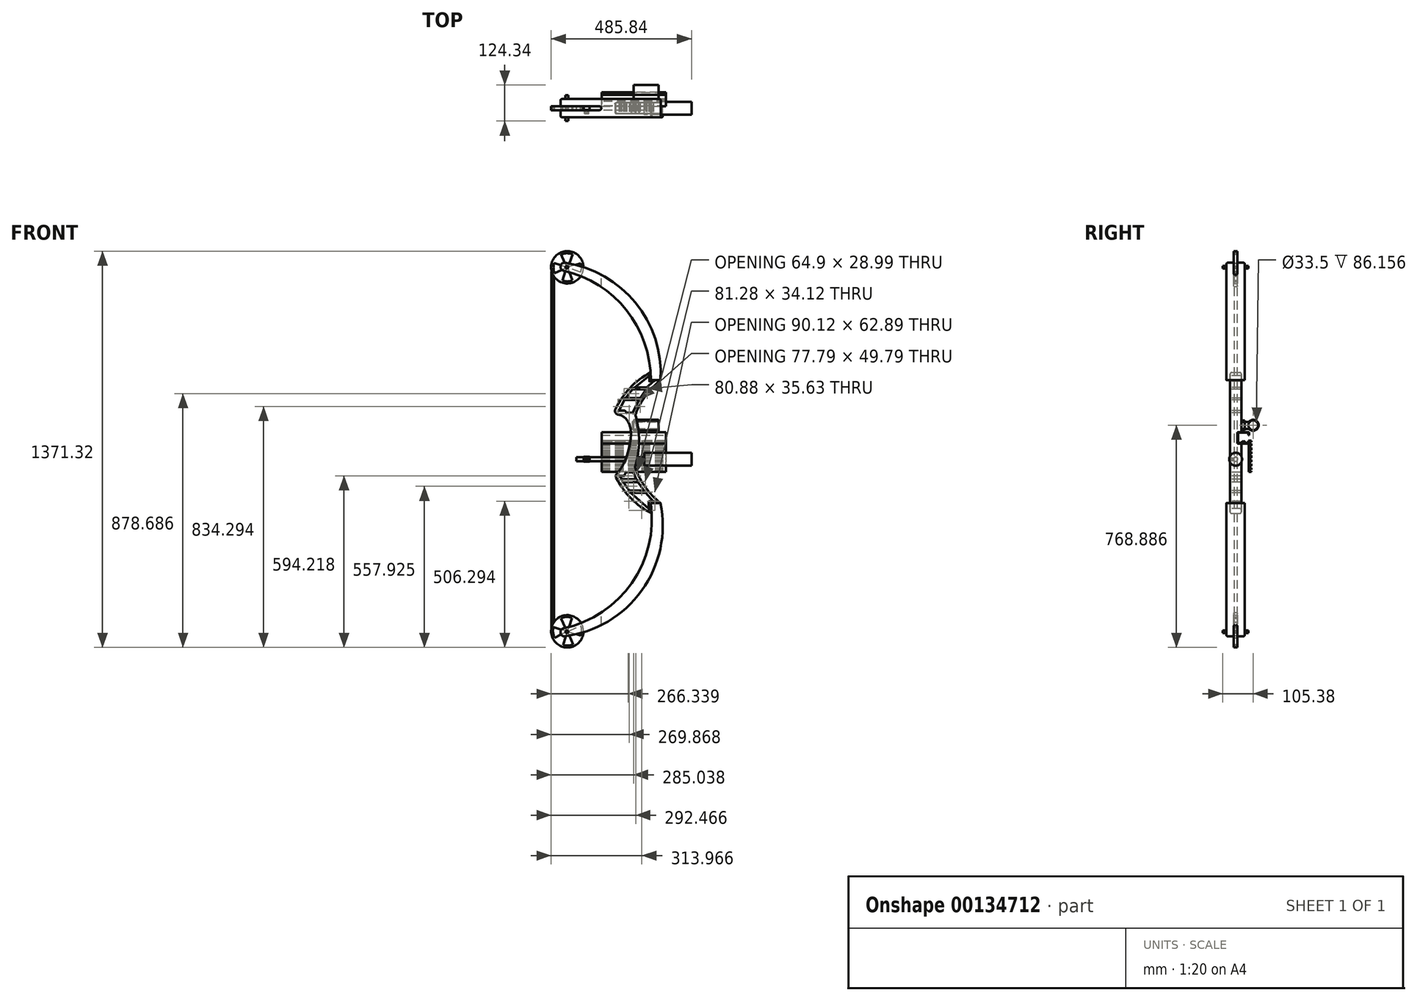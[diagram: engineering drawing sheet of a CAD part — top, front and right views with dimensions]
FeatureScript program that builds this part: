
annotation { "Feature Type Name" : "Feature", "Feature Type Description" : "" }
export const myFeature = defineFeature(function(context is Context, id is Id, definition is map)
    precondition{}
    {
        {
            var Q0;
            Q0=qCreatedBy(makeId("Front.planeOp"),FACE);
            var sketch = newSketch(context, id + "F0", { "sketchPlane" : qUnion([Q0])});
            skArc(sketch, "E0", {"start": v(312.15, 225.22) * mm, "mid": v(224.63, 471.96) * mm, "end": v(0, 606.44) * mm});
            skArc(sketch, "E1", {"start": v(0, -635.15) * mm, "mid": v(243.69, -480.2) * mm, "end": v(312.15, -199.65) * mm});
            skLineSegment(sketch, "E2", {"start": v(0, 606.44) * mm, "end": v(0, 633.37) * mm});
            skLineSegment(sketch, "E3", {"start": v(0, -635.15) * mm, "end": v(0, -662.07) * mm});
            skLineSegment(sketch, "E4", {"start": v(312.15, 225.22) * mm, "end": v(345.94, 225.22) * mm});
            skLineSegment(sketch, "E5", {"start": v(312.15, -199.65) * mm, "end": v(345.93, -199.65) * mm});
            skArc(sketch, "E6", {"start": v(345.94, 225.22) * mm, "mid": v(254.91, 498.75) * mm, "end": v(0, 633.37) * mm});
            skArc(sketch, "E7", {"start": v(0, -662.07) * mm, "mid": v(276.6, -508.4) * mm, "end": v(345.93, -199.65) * mm});
            skSolve(sketch);
        }
        {
            var Q0;
            Q0=qSketchRegion(id+"F0",true);
            extrude(context, id + "F1", {"entities" : qUnion([Q0]), "depth" : 38.1 * mm, "hasSecondDirection" : true, "secondDirectionOppositeDirection" : true, "secondDirectionDepth" : 25.4 * mm});
        }
        {
            var Q0;
            Q0=qCreatedBy(makeId("Front.planeOp"),FACE);
            var sketch = newSketch(context, id + "F2", { "sketchPlane" : qUnion([Q0])});
            skArc(sketch, "E8", {"start": v(328.65, 260.2) * mm, "mid": v(164.15, 6.75) * mm, "end": v(333.35, -243.58) * mm});
            skArc(sketch, "E9", {"start": v(345.8, 225.54) * mm, "mid": v(242.77, 13.02) * mm, "end": v(345.76, -199.52) * mm});
            skLineSegment(sketch, "E10", {"start": v(333.35, -243.58) * mm, "end": v(345.76, -199.52) * mm});
            skLineSegment(sketch, "E11", {"start": v(328.65, 260.2) * mm, "end": v(345.8, 225.54) * mm});
            skArc(sketch, "E12", {"start": v(257.5, -75.1) * mm, "mid": v(271.65, 14.65) * mm, "end": v(258.73, 104.58) * mm});
            skArc(sketch, "E13", {"start": v(176.09, -70.66) * mm, "mid": v(193.2, 15.9) * mm, "end": v(180.78, 103.27) * mm});
            skSolve(sketch);
        }
        {
            var Q0;
            Q0=qSketchRegion(id+"F2",true);
            extrude(context, id + "F3", {"entities" : qUnion([Q0]), "operationType" : NewBodyOperationType.ADD, "depth" : 25.4 * mm, "hasSecondDirection" : true, "secondDirectionOppositeDirection" : true, "secondDirectionDepth" : 13.4 * mm});
        }
        {
            var Q0;
            Q0=qSketchRegion(id+"F2",true);
            extrude(context, id + "F4", {"entities" : qUnion([Q0]), "operationType" : NewBodyOperationType.ADD, "depth" : 25.4 * mm});
        }
        {
            var Q0;
            Q0=qCreatedBy(makeId("Front.planeOp"),FACE);
            var sketch = newSketch(context, id + "F5", { "sketchPlane" : qUnion([Q0])});
            skFitSpline(sketch, "E14", {"points": [v(182.57, 103.7) * mm, v(240.87, 63.55) * mm, v(188.22, -101.45) * mm, v(156.8, -24.45) * mm, v(182.57, 103.7) * mm]});
            skSolve(sketch);
        }
        {
            var Q0;
            Q0=qSketchRegion(id+"F5",true);
            extrude(context, id + "F6", {"entities" : qUnion([Q0]), "operationType" : NewBodyOperationType.REMOVE, "oppositeDirection" : true, "depth" : 25.4 * mm, "hasSecondDirection" : true, "secondDirectionOppositeDirection" : false, "secondDirectionDepth" : 25.4 * mm});
        }
        {
            var Q0;
            {var subQ0=sQuery(id+"F2.wireOp",EDGE,"E8");Q0=makeQuery(id+"F6.boolean.opBoolean","INTERSECT",EDGE,{"disambiguationData":[OD(0.0)],"derivedFrom":[makeQuery(id+"F4.boolean.opBoolean","MERGE",FACE,{"derivedFrom":[makeQuery(id+"F3.opExtrude","SWEPT_FACE",FACE,{"disambiguationData":[OSD([subQ0])]}),makeQuery(id+"F4.opExtrude","SWEPT_FACE",FACE,{"disambiguationData":[OSD([subQ0])]})]}),makeQuery(id+"F6.opExtrude","SWEPT_FACE",FACE,{"disambiguationData":[OSD([sQuery(id+"F5.wireOp",EDGE,"E14")])]})]});}
            var Q1;
            {var subQ0=sQuery(id+"F2.wireOp",EDGE,"E8");Q1=makeQuery(id+"F6.boolean.opBoolean","INTERSECT",EDGE,{"disambiguationData":[OD(1.0)],"derivedFrom":[makeQuery(id+"F4.boolean.opBoolean","MERGE",FACE,{"derivedFrom":[makeQuery(id+"F3.opExtrude","SWEPT_FACE",FACE,{"disambiguationData":[OSD([subQ0])]}),makeQuery(id+"F4.opExtrude","SWEPT_FACE",FACE,{"disambiguationData":[OSD([subQ0])]})]}),makeQuery(id+"F6.opExtrude","SWEPT_FACE",FACE,{"disambiguationData":[OSD([sQuery(id+"F5.wireOp",EDGE,"E14")])]})]});}
            var Q2;
            {var subQ0=sQuery(id+"F2.wireOp",EDGE,"E12");var subQ1=sQuery(id+"F2.wireOp",EDGE,"E9");var subQ2=makeQuery(id+"F2.imprint","INTERSECT",VERTEX,{"disambiguationData":[OD(1.0)],"derivedFrom":[subQ1,subQ0]});Q2=makeQuery(id+"F4.boolean.opBoolean","MERGE",EDGE,{"derivedFrom":[makeQuery(id+"F3.opExtrude","SWEPT_EDGE",EDGE,{"disambiguationData":[OSD([subQ1,subQ0]),TDD([subQ2])]}),makeQuery(id+"F4.opExtrude","SWEPT_EDGE",EDGE,{"disambiguationData":[OSD([subQ1,subQ0]),TDD([subQ2])]})]});}
            var Q3;
            {var subQ0=sQuery(id+"F2.wireOp",EDGE,"E12");var subQ1=sQuery(id+"F2.wireOp",EDGE,"E9");var subQ2=makeQuery(id+"F2.imprint","INTERSECT",VERTEX,{"disambiguationData":[OD(0.0)],"derivedFrom":[subQ1,subQ0]});Q3=makeQuery(id+"F4.boolean.opBoolean","MERGE",EDGE,{"derivedFrom":[makeQuery(id+"F3.opExtrude","SWEPT_EDGE",EDGE,{"disambiguationData":[OSD([subQ1,subQ0]),TDD([subQ2])]}),makeQuery(id+"F4.opExtrude","SWEPT_EDGE",EDGE,{"disambiguationData":[OSD([subQ1,subQ0]),TDD([subQ2])]})]});}
            var Q4;
            Q4=makeQuery(id+"F1.opExtrude","SWEPT_EDGE",EDGE,{"disambiguationData":[OSD([sQuery(id+"F0.wireOp",EDGE,"E3"),sQuery(id+"F0.wireOp",EDGE,"E7")])]});
            var Q5;
            Q5=makeQuery(id+"F1.opExtrude","SWEPT_EDGE",EDGE,{"disambiguationData":[OSD([sQuery(id+"F0.wireOp",EDGE,"E1"),sQuery(id+"F0.wireOp",EDGE,"E3")])]});
            var Q6;
            Q6=makeQuery(id+"F1.opExtrude","SWEPT_EDGE",EDGE,{"disambiguationData":[OSD([sQuery(id+"F0.wireOp",EDGE,"E0"),sQuery(id+"F0.wireOp",EDGE,"E2")])]});
            var Q7;
            Q7=makeQuery(id+"F1.opExtrude","SWEPT_EDGE",EDGE,{"disambiguationData":[OSD([sQuery(id+"F0.wireOp",EDGE,"E2"),sQuery(id+"F0.wireOp",EDGE,"E6")])]});
            fillet(context, id + "F7", {"entities" : qUnion([Q0, Q1, Q2, Q3, Q4, Q5, Q6, Q7]), "radius" : 12.7 * mm, "tangentPropagation" : true, "allowEdgeOverflow" : false});
        }
        {
            var Q0;
            Q0=makeQuery(id+"F1.opExtrude","CAP_EDGE",EDGE,{"disambiguationData":[OSD([sQuery(id+"F0.wireOp",EDGE,"E0")])],"isStart":false});
            var Q1;
            Q1=makeQuery(id+"F1.opExtrude","CAP_EDGE",EDGE,{"disambiguationData":[OSD([sQuery(id+"F0.wireOp",EDGE,"E0")])],"isStart":true});
            var Q2;
            {var subQ0=sQuery(id+"F2.wireOp",EDGE,"E8");Q2=makeQuery(id+"F6.boolean.opBoolean","SPLIT",EDGE,{"disambiguationData":[TD([makeQuery(id+"F1.opExtrude","SWEPT_FACE",FACE,{"disambiguationData":[OSD([sQuery(id+"F0.wireOp",EDGE,"E0")])]})])],"derivedFrom":makeQuery(id+"F3.opExtrude","CAP_EDGE",EDGE,{"disambiguationData":[OSD([subQ0])],"isStart":true})});}
            var Q3;
            {var subQ0=sQuery(id+"F2.wireOp",EDGE,"E9");Q3=makeQuery(id+"F3.opExtrude","CAP_EDGE",EDGE,{"disambiguationData":[OSD([subQ0]),TDD([makeQuery(id+"F2.imprint","IMPRINT",EDGE,{"disambiguationData":[TD([[makeQuery(id+"F2.imprint","INTERSECT",VERTEX,{"derivedFrom":[subQ0,sQuery(id+"F2.wireOp",EDGE,"E11")]}),-1.0]])],"derivedFrom":subQ0})])],"isStart":true});}
            var Q4;
            {var subQ0=sQuery(id+"F2.wireOp",EDGE,"E8");Q4=makeQuery(id+"F6.boolean.opBoolean","SPLIT",EDGE,{"disambiguationData":[TD([makeQuery(id+"F1.opExtrude","SWEPT_FACE",FACE,{"disambiguationData":[OSD([sQuery(id+"F0.wireOp",EDGE,"E0")])]})])],"derivedFrom":makeQuery(id+"F3.opExtrude","CAP_EDGE",EDGE,{"disambiguationData":[OSD([subQ0])],"isStart":false})});}
            var Q5;
            {var subQ0=sQuery(id+"F2.wireOp",EDGE,"E9");Q5=makeQuery(id+"F3.opExtrude","CAP_EDGE",EDGE,{"disambiguationData":[OSD([subQ0]),TDD([makeQuery(id+"F2.imprint","IMPRINT",EDGE,{"disambiguationData":[TD([[makeQuery(id+"F2.imprint","INTERSECT",VERTEX,{"derivedFrom":[subQ0,sQuery(id+"F2.wireOp",EDGE,"E11")]}),-1.0]])],"derivedFrom":subQ0})])],"isStart":false});}
            var Q6;
            Q6=makeQuery(id+"F1.opExtrude","CAP_EDGE",EDGE,{"disambiguationData":[OSD([sQuery(id+"F0.wireOp",EDGE,"E1")])],"isStart":true});
            var Q7;
            Q7=makeQuery(id+"F1.opExtrude","CAP_EDGE",EDGE,{"disambiguationData":[OSD([sQuery(id+"F0.wireOp",EDGE,"E1")])],"isStart":false});
            fillet(context, id + "F8", {"entities" : qUnion([Q0, Q1, Q2, Q3, Q4, Q5, Q6, Q7]), "radius" : 5.08 * mm, "tangentPropagation" : true, "allowEdgeOverflow" : false});
        }
        {
            var Q0;
            Q0=qCreatedBy(makeId("Top.planeOp"),FACE);
            var sketch = newSketch(context, id + "F9", { "sketchPlane" : qUnion([Q0])});
            skLineSegment(sketch, "E15", {"start": v(0, 0) * mm, "end": v(134.72, 0) * mm});
            skLineSegment(sketch, "E16", {"start": v(0, -12.95) * mm, "end": v(134.72, -12.95) * mm});
            skArc(sketch, "E17", {"start": v(134.72, -12.95) * mm, "mid": v(141.2, -6.48) * mm, "end": v(134.72, 0) * mm});
            skLineSegment(sketch, "E18", {"start": v(0, 0) * mm, "end": v(0, -12.95) * mm});
            skSolve(sketch);
        }
        {
            var Q0;
            Q0=qSketchRegion(id+"F9",true);
            extrude(context, id + "F10", {"entities" : qUnion([Q0]), "operationType" : NewBodyOperationType.REMOVE, "oppositeDirection" : true, "depth" : 1043.23 * mm, "hasSecondDirection" : true, "secondDirectionOppositeDirection" : false, "secondDirectionDepth" : 725.43 * mm});
        }
        {
            var Q0;
            Q0=qCreatedBy(makeId("Front.planeOp"),FACE);
            var sketch = newSketch(context, id + "F11", { "sketchPlane" : qUnion([Q0])});
            skLineSegment(sketch, "E19", {"start": v(307.3, 240.65) * mm, "end": v(307.3, 221.5) * mm});
            skLineSegment(sketch, "E20", {"start": v(307.3, 221.5) * mm, "end": v(321.6, 221.5) * mm});
            skLineSegment(sketch, "E21", {"start": v(321.6, 221.5) * mm, "end": v(299.17, 200.17) * mm});
            skLineSegment(sketch, "E22", {"start": v(299.17, 200.17) * mm, "end": v(257.15, 200.17) * mm});
            skLineSegment(sketch, "E23", {"start": v(257.15, 200.17) * mm, "end": v(307.3, 240.65) * mm});
            skLineSegment(sketch, "E24", {"start": v(249.41, 194.56) * mm, "end": v(295.62, 194.56) * mm});
            skLineSegment(sketch, "E25", {"start": v(295.62, 194.56) * mm, "end": v(275.44, 164.01) * mm});
            skLineSegment(sketch, "E26", {"start": v(275.44, 164.01) * mm, "end": v(224.78, 164.01) * mm});
            skLineSegment(sketch, "E27", {"start": v(224.78, 164.01) * mm, "end": v(249.41, 194.56) * mm});
            skLineSegment(sketch, "E28", {"start": v(221.45, 157.23) * mm, "end": v(202.6, 120.92) * mm});
            skLineSegment(sketch, "E29", {"start": v(202.6, 120.92) * mm, "end": v(222.32, 120.92) * mm});
            skLineSegment(sketch, "E30", {"start": v(222.32, 120.92) * mm, "end": v(228.43, 112.54) * mm});
            skLineSegment(sketch, "E31", {"start": v(228.43, 112.54) * mm, "end": v(249.56, 112.54) * mm});
            skLineSegment(sketch, "E32", {"start": v(249.56, 112.54) * mm, "end": v(272.08, 156.7) * mm});
            skLineSegment(sketch, "E33", {"start": v(272.08, 156.7) * mm, "end": v(221.45, 157.23) * mm});
            skSolve(sketch);
        }
        {
            var Q0;
            Q0=qSketchRegion(id+"F11",true);
            extrude(context, id + "F12", {"entities" : qUnion([Q0]), "operationType" : NewBodyOperationType.REMOVE, "oppositeDirection" : true, "depth" : 25.4 * mm, "hasSecondDirection" : true, "secondDirectionOppositeDirection" : false, "secondDirectionDepth" : 103.34 * mm});
        }
        {
            var Q0;
            Q0=qCreatedBy(makeId("Front.planeOp"),FACE);
            var sketch = newSketch(context, id + "F13", { "sketchPlane" : qUnion([Q0])});
            skLineSegment(sketch, "E34", {"start": v(304.9, -218.91) * mm, "end": v(304.9, -193.2) * mm});
            skLineSegment(sketch, "E35", {"start": v(304.9, -193.2) * mm, "end": v(320.72, -193.2) * mm});
            skLineSegment(sketch, "E36", {"start": v(320.72, -193.2) * mm, "end": v(294.36, -164.2) * mm});
            skLineSegment(sketch, "E37", {"start": v(294.36, -164.2) * mm, "end": v(243.05, -164.2) * mm});
            skLineSegment(sketch, "E38", {"start": v(243.05, -164.2) * mm, "end": v(304.9, -218.91) * mm});
            skLineSegment(sketch, "E39", {"start": v(288.23, -156) * mm, "end": v(237.22, -156) * mm});
            skLineSegment(sketch, "E40", {"start": v(237.22, -156) * mm, "end": v(216.74, -126.96) * mm});
            skLineSegment(sketch, "E41", {"start": v(216.74, -126.96) * mm, "end": v(267.82, -126.96) * mm});
            skLineSegment(sketch, "E42", {"start": v(267.82, -126.96) * mm, "end": v(288.23, -156) * mm});
            skLineSegment(sketch, "E43", {"start": v(262.27, -117.14) * mm, "end": v(210.93, -117.14) * mm});
            skLineSegment(sketch, "E44", {"start": v(210.93, -117.14) * mm, "end": v(205.44, -106.16) * mm});
            skLineSegment(sketch, "E45", {"start": v(205.44, -106.16) * mm, "end": v(220.33, -106.16) * mm});
            skLineSegment(sketch, "E46", {"start": v(220.33, -106.16) * mm, "end": v(226.6, -93.23) * mm});
            skLineSegment(sketch, "E47", {"start": v(226.6, -93.23) * mm, "end": v(251.3, -93.23) * mm});
            skLineSegment(sketch, "E48", {"start": v(251.3, -93.23) * mm, "end": v(262.27, -117.14) * mm});
            skSolve(sketch);
        }
        {
            var Q0;
            Q0=qSketchRegion(id+"F13",true);
            extrude(context, id + "F14", {"entities" : qUnion([Q0]), "operationType" : NewBodyOperationType.REMOVE, "oppositeDirection" : true, "depth" : 25.4 * mm, "hasSecondDirection" : true, "secondDirectionOppositeDirection" : false, "secondDirectionDepth" : 136.26 * mm});
        }
        {
            var Q0;
            Q0=qCreatedBy(makeId("Front.planeOp"),FACE);
            var sketch = newSketch(context, id + "F15", { "sketchPlane" : qUnion([Q0])});
            skCircle(sketch, "E49", {"center": v(23.33, 616.03) * mm, "radius": 55.9 * mm});
            skCircle(sketch, "E50", {"center": v(23.33, -643.5) * mm, "radius": 55.9 * mm});
            skCircle(sketch, "E51", {"center": v(23.33, 616.03) * mm, "radius": 4.58 * mm});
            skLineSegment(sketch, "E52", {"start": v(19.88, 619.04) * mm, "end": v(2.06, 661.07) * mm});
            skLineSegment(sketch, "E53", {"start": v(26.37, 619.46) * mm, "end": v(42.28, 661.63) * mm});
            skLineSegment(sketch, "E54", {"start": v(20.5, 612.42) * mm, "end": v(6.51, 570.45) * mm});
            skLineSegment(sketch, "E55", {"start": v(26.38, 612.6) * mm, "end": v(40.24, 570.82) * mm});
            skArc(sketch, "E56", {"start": v(42.28, 661.63) * mm, "mid": v(22.13, 664.6) * mm, "end": v(2.06, 661.07) * mm});
            skArc(sketch, "E57", {"start": v(6.51, 570.45) * mm, "mid": v(23.42, 566.64) * mm, "end": v(40.24, 570.82) * mm});
            skLineSegment(sketch, "E58", {"start": v(27.5, 617.94) * mm, "end": v(69.87, 630.2) * mm});
            skLineSegment(sketch, "E59", {"start": v(27.5, 614.11) * mm, "end": v(69.21, 598.67) * mm});
            skLineSegment(sketch, "E60", {"start": v(19.14, 617.87) * mm, "end": v(-22.68, 630.88) * mm});
            skLineSegment(sketch, "E61", {"start": v(19.1, 614.26) * mm, "end": v(-21.29, 595.17) * mm});
            skArc(sketch, "E62", {"start": v(-22.68, 630.88) * mm, "mid": v(-24.57, 612.92) * mm, "end": v(-21.29, 595.17) * mm});
            skArc(sketch, "E63", {"start": v(69.21, 598.67) * mm, "mid": v(72.24, 614.38) * mm, "end": v(69.87, 630.2) * mm});
            skCircle(sketch, "E64", {"center": v(23.33, -643.5) * mm, "radius": 4.58 * mm});
            skLineSegment(sketch, "E65", {"start": v(20.29, -640.08) * mm, "end": v(1.41, -598.57) * mm});
            skLineSegment(sketch, "E66", {"start": v(25.93, -639.73) * mm, "end": v(39.75, -596.96) * mm});
            skLineSegment(sketch, "E67", {"start": v(21.54, -647.73) * mm, "end": v(8.9, -690.96) * mm});
            skLineSegment(sketch, "E68", {"start": v(26, -647.23) * mm, "end": v(44, -688.73) * mm});
            skLineSegment(sketch, "E69", {"start": v(27.8, -642.46) * mm, "end": v(69.69, -624.26) * mm});
            skLineSegment(sketch, "E70", {"start": v(27.47, -645.49) * mm, "end": v(70.34, -658.33) * mm});
            skLineSegment(sketch, "E71", {"start": v(18.96, -642.13) * mm, "end": v(-24.47, -629.13) * mm});
            skLineSegment(sketch, "E72", {"start": v(19.17, -645.42) * mm, "end": v(-19.95, -665.33) * mm});
            skArc(sketch, "E73", {"start": v(39.75, -596.96) * mm, "mid": v(20.4, -593.5) * mm, "end": v(1.41, -598.57) * mm});
            skArc(sketch, "E74", {"start": v(-24.47, -629.13) * mm, "mid": v(-25.69, -647.66) * mm, "end": v(-19.95, -665.33) * mm});
            skArc(sketch, "E75", {"start": v(8.9, -690.96) * mm, "mid": v(26.64, -692.84) * mm, "end": v(44, -688.73) * mm});
            skArc(sketch, "E76", {"start": v(70.34, -658.33) * mm, "mid": v(73.15, -641.24) * mm, "end": v(69.69, -624.26) * mm});
            skSolve(sketch);
        }
        {
            var Q0;
            Q0=qCreatedBy(makeId("Front.planeOp"),FACE);
            var sketch = newSketch(context, id + "F16", { "sketchPlane" : qUnion([Q0])});
            skCircle(sketch, "E77", {"center": v(21.85, 616.5) * mm, "radius": 4.59 * mm});
            skCircle(sketch, "E78", {"center": v(21.85, -645.2) * mm, "radius": 4.58 * mm});
            skSolve(sketch);
        }
        {
            var Q0;
            Q0=qSketchRegion(id+"F16",true);
            extrude(context, id + "F17", {"entities" : qUnion([Q0]), "operationType" : NewBodyOperationType.ADD, "depth" : 50.8 * mm, "hasSecondDirection" : true, "secondDirectionOppositeDirection" : true, "secondDirectionDepth" : 38.1 * mm});
        }
        {
            var Q0;
            Q0=makeQuery(id+"F12.boolean.opBoolean","INTERSECT",EDGE,{"derivedFrom":[makeQuery(id+"F3.opExtrude","CAP_FACE",FACE,{"disambiguationData":[OSD([sQuery(id+"F2.wireOp",EDGE,"E8"),sQuery(id+"F2.wireOp",EDGE,"E9"),sQuery(id+"F2.wireOp",EDGE,"E10"),sQuery(id+"F2.wireOp",EDGE,"E11"),sQuery(id+"F2.wireOp",EDGE,"E12")])],"isStart":false}),makeQuery(id+"F12.opExtrude","SWEPT_FACE",FACE,{"disambiguationData":[OSD([sQuery(id+"F11.wireOp",EDGE,"E26")])]})]});
            var Q1;
            Q1=makeQuery(id+"F12.boolean.opBoolean","INTERSECT",EDGE,{"derivedFrom":[makeQuery(id+"F3.opExtrude","CAP_FACE",FACE,{"disambiguationData":[OSD([sQuery(id+"F2.wireOp",EDGE,"E8"),sQuery(id+"F2.wireOp",EDGE,"E9"),sQuery(id+"F2.wireOp",EDGE,"E10"),sQuery(id+"F2.wireOp",EDGE,"E11"),sQuery(id+"F2.wireOp",EDGE,"E12")])],"isStart":false}),makeQuery(id+"F12.opExtrude","SWEPT_FACE",FACE,{"disambiguationData":[OSD([sQuery(id+"F11.wireOp",EDGE,"E31")])]})]});
            var Q2;
            Q2=makeQuery(id+"F12.boolean.opBoolean","INTERSECT",EDGE,{"derivedFrom":[makeQuery(id+"F3.opExtrude","CAP_FACE",FACE,{"disambiguationData":[OSD([sQuery(id+"F2.wireOp",EDGE,"E8"),sQuery(id+"F2.wireOp",EDGE,"E9"),sQuery(id+"F2.wireOp",EDGE,"E10"),sQuery(id+"F2.wireOp",EDGE,"E11"),sQuery(id+"F2.wireOp",EDGE,"E12")])],"isStart":false}),makeQuery(id+"F12.opExtrude","SWEPT_FACE",FACE,{"disambiguationData":[OSD([sQuery(id+"F11.wireOp",EDGE,"E30")])]})]});
            var Q3;
            Q3=makeQuery(id+"F12.boolean.opBoolean","INTERSECT",EDGE,{"derivedFrom":[makeQuery(id+"F3.opExtrude","CAP_FACE",FACE,{"disambiguationData":[OSD([sQuery(id+"F2.wireOp",EDGE,"E8"),sQuery(id+"F2.wireOp",EDGE,"E9"),sQuery(id+"F2.wireOp",EDGE,"E10"),sQuery(id+"F2.wireOp",EDGE,"E11"),sQuery(id+"F2.wireOp",EDGE,"E12")])],"isStart":false}),makeQuery(id+"F12.opExtrude","SWEPT_FACE",FACE,{"disambiguationData":[OSD([sQuery(id+"F11.wireOp",EDGE,"E29")])]})]});
            var Q4;
            Q4=makeQuery(id+"F12.boolean.opBoolean","INTERSECT",EDGE,{"derivedFrom":[makeQuery(id+"F3.opExtrude","CAP_FACE",FACE,{"disambiguationData":[OSD([sQuery(id+"F2.wireOp",EDGE,"E8"),sQuery(id+"F2.wireOp",EDGE,"E9"),sQuery(id+"F2.wireOp",EDGE,"E10"),sQuery(id+"F2.wireOp",EDGE,"E11"),sQuery(id+"F2.wireOp",EDGE,"E12")])],"isStart":false}),makeQuery(id+"F12.opExtrude","SWEPT_FACE",FACE,{"disambiguationData":[OSD([sQuery(id+"F11.wireOp",EDGE,"E32")])]})]});
            var Q5;
            Q5=makeQuery(id+"F12.boolean.opBoolean","INTERSECT",EDGE,{"derivedFrom":[makeQuery(id+"F3.opExtrude","CAP_FACE",FACE,{"disambiguationData":[OSD([sQuery(id+"F2.wireOp",EDGE,"E8"),sQuery(id+"F2.wireOp",EDGE,"E9"),sQuery(id+"F2.wireOp",EDGE,"E10"),sQuery(id+"F2.wireOp",EDGE,"E11"),sQuery(id+"F2.wireOp",EDGE,"E12")])],"isStart":false}),makeQuery(id+"F12.opExtrude","SWEPT_FACE",FACE,{"disambiguationData":[OSD([sQuery(id+"F11.wireOp",EDGE,"E33")])]})]});
            var Q6;
            Q6=makeQuery(id+"F12.boolean.opBoolean","INTERSECT",EDGE,{"derivedFrom":[makeQuery(id+"F3.opExtrude","CAP_FACE",FACE,{"disambiguationData":[OSD([sQuery(id+"F2.wireOp",EDGE,"E8"),sQuery(id+"F2.wireOp",EDGE,"E9"),sQuery(id+"F2.wireOp",EDGE,"E10"),sQuery(id+"F2.wireOp",EDGE,"E11"),sQuery(id+"F2.wireOp",EDGE,"E12")])],"isStart":false}),makeQuery(id+"F12.opExtrude","SWEPT_FACE",FACE,{"disambiguationData":[OSD([sQuery(id+"F11.wireOp",EDGE,"E28")])]})]});
            var Q7;
            Q7=makeQuery(id+"F12.boolean.opBoolean","INTERSECT",EDGE,{"derivedFrom":[makeQuery(id+"F3.opExtrude","CAP_FACE",FACE,{"disambiguationData":[OSD([sQuery(id+"F2.wireOp",EDGE,"E8"),sQuery(id+"F2.wireOp",EDGE,"E9"),sQuery(id+"F2.wireOp",EDGE,"E10"),sQuery(id+"F2.wireOp",EDGE,"E11"),sQuery(id+"F2.wireOp",EDGE,"E12")])],"isStart":false}),makeQuery(id+"F12.opExtrude","SWEPT_FACE",FACE,{"disambiguationData":[OSD([sQuery(id+"F11.wireOp",EDGE,"E25")])]})]});
            var Q8;
            Q8=makeQuery(id+"F12.boolean.opBoolean","INTERSECT",EDGE,{"derivedFrom":[makeQuery(id+"F3.opExtrude","CAP_FACE",FACE,{"disambiguationData":[OSD([sQuery(id+"F2.wireOp",EDGE,"E8"),sQuery(id+"F2.wireOp",EDGE,"E9"),sQuery(id+"F2.wireOp",EDGE,"E10"),sQuery(id+"F2.wireOp",EDGE,"E11"),sQuery(id+"F2.wireOp",EDGE,"E12")])],"isStart":false}),makeQuery(id+"F12.opExtrude","SWEPT_FACE",FACE,{"disambiguationData":[OSD([sQuery(id+"F11.wireOp",EDGE,"E24")])]})]});
            var Q9;
            Q9=makeQuery(id+"F12.boolean.opBoolean","INTERSECT",EDGE,{"derivedFrom":[makeQuery(id+"F3.opExtrude","CAP_FACE",FACE,{"disambiguationData":[OSD([sQuery(id+"F2.wireOp",EDGE,"E8"),sQuery(id+"F2.wireOp",EDGE,"E9"),sQuery(id+"F2.wireOp",EDGE,"E10"),sQuery(id+"F2.wireOp",EDGE,"E11"),sQuery(id+"F2.wireOp",EDGE,"E12")])],"isStart":false}),makeQuery(id+"F12.opExtrude","SWEPT_FACE",FACE,{"disambiguationData":[OSD([sQuery(id+"F11.wireOp",EDGE,"E27")])]})]});
            var Q10;
            Q10=makeQuery(id+"F12.boolean.opBoolean","INTERSECT",EDGE,{"derivedFrom":[makeQuery(id+"F3.opExtrude","CAP_FACE",FACE,{"disambiguationData":[OSD([sQuery(id+"F2.wireOp",EDGE,"E8"),sQuery(id+"F2.wireOp",EDGE,"E9"),sQuery(id+"F2.wireOp",EDGE,"E10"),sQuery(id+"F2.wireOp",EDGE,"E11"),sQuery(id+"F2.wireOp",EDGE,"E12")])],"isStart":false}),makeQuery(id+"F12.opExtrude","SWEPT_FACE",FACE,{"disambiguationData":[OSD([sQuery(id+"F11.wireOp",EDGE,"E22")])]})]});
            var Q11;
            Q11=makeQuery(id+"F12.boolean.opBoolean","INTERSECT",EDGE,{"derivedFrom":[makeQuery(id+"F3.opExtrude","CAP_FACE",FACE,{"disambiguationData":[OSD([sQuery(id+"F2.wireOp",EDGE,"E8"),sQuery(id+"F2.wireOp",EDGE,"E9"),sQuery(id+"F2.wireOp",EDGE,"E10"),sQuery(id+"F2.wireOp",EDGE,"E11"),sQuery(id+"F2.wireOp",EDGE,"E12")])],"isStart":false}),makeQuery(id+"F12.opExtrude","SWEPT_FACE",FACE,{"disambiguationData":[OSD([sQuery(id+"F11.wireOp",EDGE,"E21")])]})]});
            var Q12;
            Q12=makeQuery(id+"F12.boolean.opBoolean","INTERSECT",EDGE,{"derivedFrom":[makeQuery(id+"F3.opExtrude","CAP_FACE",FACE,{"disambiguationData":[OSD([sQuery(id+"F2.wireOp",EDGE,"E8"),sQuery(id+"F2.wireOp",EDGE,"E9"),sQuery(id+"F2.wireOp",EDGE,"E10"),sQuery(id+"F2.wireOp",EDGE,"E11"),sQuery(id+"F2.wireOp",EDGE,"E12")])],"isStart":false}),makeQuery(id+"F12.opExtrude","SWEPT_FACE",FACE,{"disambiguationData":[OSD([sQuery(id+"F11.wireOp",EDGE,"E20")])]})]});
            var Q13;
            Q13=makeQuery(id+"F12.boolean.opBoolean","INTERSECT",EDGE,{"derivedFrom":[makeQuery(id+"F3.opExtrude","CAP_FACE",FACE,{"disambiguationData":[OSD([sQuery(id+"F2.wireOp",EDGE,"E8"),sQuery(id+"F2.wireOp",EDGE,"E9"),sQuery(id+"F2.wireOp",EDGE,"E10"),sQuery(id+"F2.wireOp",EDGE,"E11"),sQuery(id+"F2.wireOp",EDGE,"E12")])],"isStart":false}),makeQuery(id+"F12.opExtrude","SWEPT_FACE",FACE,{"disambiguationData":[OSD([sQuery(id+"F11.wireOp",EDGE,"E19")])]})]});
            var Q14;
            Q14=makeQuery(id+"F12.boolean.opBoolean","INTERSECT",EDGE,{"derivedFrom":[makeQuery(id+"F3.opExtrude","CAP_FACE",FACE,{"disambiguationData":[OSD([sQuery(id+"F2.wireOp",EDGE,"E8"),sQuery(id+"F2.wireOp",EDGE,"E9"),sQuery(id+"F2.wireOp",EDGE,"E10"),sQuery(id+"F2.wireOp",EDGE,"E11"),sQuery(id+"F2.wireOp",EDGE,"E12")])],"isStart":false}),makeQuery(id+"F12.opExtrude","SWEPT_FACE",FACE,{"disambiguationData":[OSD([sQuery(id+"F11.wireOp",EDGE,"E23")])]})]});
            var Q15;
            Q15=makeQuery(id+"F12.boolean.opBoolean","INTERSECT",EDGE,{"derivedFrom":[makeQuery(id+"F3.opExtrude","CAP_FACE",FACE,{"disambiguationData":[OSD([sQuery(id+"F2.wireOp",EDGE,"E8"),sQuery(id+"F2.wireOp",EDGE,"E9"),sQuery(id+"F2.wireOp",EDGE,"E10"),sQuery(id+"F2.wireOp",EDGE,"E11"),sQuery(id+"F2.wireOp",EDGE,"E12")])],"isStart":true}),makeQuery(id+"F12.opExtrude","SWEPT_FACE",FACE,{"disambiguationData":[OSD([sQuery(id+"F11.wireOp",EDGE,"E31")])]})]});
            var Q16;
            Q16=makeQuery(id+"F12.boolean.opBoolean","INTERSECT",EDGE,{"derivedFrom":[makeQuery(id+"F3.opExtrude","CAP_FACE",FACE,{"disambiguationData":[OSD([sQuery(id+"F2.wireOp",EDGE,"E8"),sQuery(id+"F2.wireOp",EDGE,"E9"),sQuery(id+"F2.wireOp",EDGE,"E10"),sQuery(id+"F2.wireOp",EDGE,"E11"),sQuery(id+"F2.wireOp",EDGE,"E12")])],"isStart":true}),makeQuery(id+"F12.opExtrude","SWEPT_FACE",FACE,{"disambiguationData":[OSD([sQuery(id+"F11.wireOp",EDGE,"E30")])]})]});
            var Q17;
            Q17=makeQuery(id+"F12.boolean.opBoolean","INTERSECT",EDGE,{"derivedFrom":[makeQuery(id+"F3.opExtrude","CAP_FACE",FACE,{"disambiguationData":[OSD([sQuery(id+"F2.wireOp",EDGE,"E8"),sQuery(id+"F2.wireOp",EDGE,"E9"),sQuery(id+"F2.wireOp",EDGE,"E10"),sQuery(id+"F2.wireOp",EDGE,"E11"),sQuery(id+"F2.wireOp",EDGE,"E12")])],"isStart":true}),makeQuery(id+"F12.opExtrude","SWEPT_FACE",FACE,{"disambiguationData":[OSD([sQuery(id+"F11.wireOp",EDGE,"E29")])]})]});
            var Q18;
            Q18=makeQuery(id+"F12.boolean.opBoolean","INTERSECT",EDGE,{"derivedFrom":[makeQuery(id+"F3.opExtrude","CAP_FACE",FACE,{"disambiguationData":[OSD([sQuery(id+"F2.wireOp",EDGE,"E8"),sQuery(id+"F2.wireOp",EDGE,"E9"),sQuery(id+"F2.wireOp",EDGE,"E10"),sQuery(id+"F2.wireOp",EDGE,"E11"),sQuery(id+"F2.wireOp",EDGE,"E12")])],"isStart":true}),makeQuery(id+"F12.opExtrude","SWEPT_FACE",FACE,{"disambiguationData":[OSD([sQuery(id+"F11.wireOp",EDGE,"E28")])]})]});
            var Q19;
            Q19=makeQuery(id+"F12.boolean.opBoolean","INTERSECT",EDGE,{"derivedFrom":[makeQuery(id+"F3.opExtrude","CAP_FACE",FACE,{"disambiguationData":[OSD([sQuery(id+"F2.wireOp",EDGE,"E8"),sQuery(id+"F2.wireOp",EDGE,"E9"),sQuery(id+"F2.wireOp",EDGE,"E10"),sQuery(id+"F2.wireOp",EDGE,"E11"),sQuery(id+"F2.wireOp",EDGE,"E12")])],"isStart":true}),makeQuery(id+"F12.opExtrude","SWEPT_FACE",FACE,{"disambiguationData":[OSD([sQuery(id+"F11.wireOp",EDGE,"E33")])]})]});
            var Q20;
            Q20=makeQuery(id+"F12.boolean.opBoolean","INTERSECT",EDGE,{"derivedFrom":[makeQuery(id+"F3.opExtrude","CAP_FACE",FACE,{"disambiguationData":[OSD([sQuery(id+"F2.wireOp",EDGE,"E8"),sQuery(id+"F2.wireOp",EDGE,"E9"),sQuery(id+"F2.wireOp",EDGE,"E10"),sQuery(id+"F2.wireOp",EDGE,"E11"),sQuery(id+"F2.wireOp",EDGE,"E12")])],"isStart":true}),makeQuery(id+"F12.opExtrude","SWEPT_FACE",FACE,{"disambiguationData":[OSD([sQuery(id+"F11.wireOp",EDGE,"E32")])]})]});
            var Q21;
            Q21=makeQuery(id+"F12.boolean.opBoolean","INTERSECT",EDGE,{"derivedFrom":[makeQuery(id+"F3.opExtrude","CAP_FACE",FACE,{"disambiguationData":[OSD([sQuery(id+"F2.wireOp",EDGE,"E8"),sQuery(id+"F2.wireOp",EDGE,"E9"),sQuery(id+"F2.wireOp",EDGE,"E10"),sQuery(id+"F2.wireOp",EDGE,"E11"),sQuery(id+"F2.wireOp",EDGE,"E12")])],"isStart":true}),makeQuery(id+"F12.opExtrude","SWEPT_FACE",FACE,{"disambiguationData":[OSD([sQuery(id+"F11.wireOp",EDGE,"E25")])]})]});
            var Q22;
            Q22=makeQuery(id+"F12.boolean.opBoolean","INTERSECT",EDGE,{"derivedFrom":[makeQuery(id+"F3.opExtrude","CAP_FACE",FACE,{"disambiguationData":[OSD([sQuery(id+"F2.wireOp",EDGE,"E8"),sQuery(id+"F2.wireOp",EDGE,"E9"),sQuery(id+"F2.wireOp",EDGE,"E10"),sQuery(id+"F2.wireOp",EDGE,"E11"),sQuery(id+"F2.wireOp",EDGE,"E12")])],"isStart":true}),makeQuery(id+"F12.opExtrude","SWEPT_FACE",FACE,{"disambiguationData":[OSD([sQuery(id+"F11.wireOp",EDGE,"E26")])]})]});
            var Q23;
            Q23=makeQuery(id+"F12.boolean.opBoolean","INTERSECT",EDGE,{"derivedFrom":[makeQuery(id+"F3.opExtrude","CAP_FACE",FACE,{"disambiguationData":[OSD([sQuery(id+"F2.wireOp",EDGE,"E8"),sQuery(id+"F2.wireOp",EDGE,"E9"),sQuery(id+"F2.wireOp",EDGE,"E10"),sQuery(id+"F2.wireOp",EDGE,"E11"),sQuery(id+"F2.wireOp",EDGE,"E12")])],"isStart":true}),makeQuery(id+"F12.opExtrude","SWEPT_FACE",FACE,{"disambiguationData":[OSD([sQuery(id+"F11.wireOp",EDGE,"E27")])]})]});
            var Q24;
            Q24=makeQuery(id+"F12.boolean.opBoolean","INTERSECT",EDGE,{"derivedFrom":[makeQuery(id+"F3.opExtrude","CAP_FACE",FACE,{"disambiguationData":[OSD([sQuery(id+"F2.wireOp",EDGE,"E8"),sQuery(id+"F2.wireOp",EDGE,"E9"),sQuery(id+"F2.wireOp",EDGE,"E10"),sQuery(id+"F2.wireOp",EDGE,"E11"),sQuery(id+"F2.wireOp",EDGE,"E12")])],"isStart":true}),makeQuery(id+"F12.opExtrude","SWEPT_FACE",FACE,{"disambiguationData":[OSD([sQuery(id+"F11.wireOp",EDGE,"E24")])]})]});
            var Q25;
            Q25=makeQuery(id+"F12.boolean.opBoolean","INTERSECT",EDGE,{"derivedFrom":[makeQuery(id+"F3.opExtrude","CAP_FACE",FACE,{"disambiguationData":[OSD([sQuery(id+"F2.wireOp",EDGE,"E8"),sQuery(id+"F2.wireOp",EDGE,"E9"),sQuery(id+"F2.wireOp",EDGE,"E10"),sQuery(id+"F2.wireOp",EDGE,"E11"),sQuery(id+"F2.wireOp",EDGE,"E12")])],"isStart":true}),makeQuery(id+"F12.opExtrude","SWEPT_FACE",FACE,{"disambiguationData":[OSD([sQuery(id+"F11.wireOp",EDGE,"E22")])]})]});
            var Q26;
            Q26=makeQuery(id+"F12.boolean.opBoolean","INTERSECT",EDGE,{"derivedFrom":[makeQuery(id+"F3.opExtrude","CAP_FACE",FACE,{"disambiguationData":[OSD([sQuery(id+"F2.wireOp",EDGE,"E8"),sQuery(id+"F2.wireOp",EDGE,"E9"),sQuery(id+"F2.wireOp",EDGE,"E10"),sQuery(id+"F2.wireOp",EDGE,"E11"),sQuery(id+"F2.wireOp",EDGE,"E12")])],"isStart":true}),makeQuery(id+"F12.opExtrude","SWEPT_FACE",FACE,{"disambiguationData":[OSD([sQuery(id+"F11.wireOp",EDGE,"E21")])]})]});
            var Q27;
            Q27=makeQuery(id+"F12.boolean.opBoolean","INTERSECT",EDGE,{"derivedFrom":[makeQuery(id+"F3.opExtrude","CAP_FACE",FACE,{"disambiguationData":[OSD([sQuery(id+"F2.wireOp",EDGE,"E8"),sQuery(id+"F2.wireOp",EDGE,"E9"),sQuery(id+"F2.wireOp",EDGE,"E10"),sQuery(id+"F2.wireOp",EDGE,"E11"),sQuery(id+"F2.wireOp",EDGE,"E12")])],"isStart":true}),makeQuery(id+"F12.opExtrude","SWEPT_FACE",FACE,{"disambiguationData":[OSD([sQuery(id+"F11.wireOp",EDGE,"E23")])]})]});
            var Q28;
            Q28=makeQuery(id+"F12.boolean.opBoolean","INTERSECT",EDGE,{"derivedFrom":[makeQuery(id+"F3.opExtrude","CAP_FACE",FACE,{"disambiguationData":[OSD([sQuery(id+"F2.wireOp",EDGE,"E8"),sQuery(id+"F2.wireOp",EDGE,"E9"),sQuery(id+"F2.wireOp",EDGE,"E10"),sQuery(id+"F2.wireOp",EDGE,"E11"),sQuery(id+"F2.wireOp",EDGE,"E12")])],"isStart":true}),makeQuery(id+"F12.opExtrude","SWEPT_FACE",FACE,{"disambiguationData":[OSD([sQuery(id+"F11.wireOp",EDGE,"E20")])]})]});
            var Q29;
            Q29=makeQuery(id+"F12.boolean.opBoolean","INTERSECT",EDGE,{"derivedFrom":[makeQuery(id+"F3.opExtrude","CAP_FACE",FACE,{"disambiguationData":[OSD([sQuery(id+"F2.wireOp",EDGE,"E8"),sQuery(id+"F2.wireOp",EDGE,"E9"),sQuery(id+"F2.wireOp",EDGE,"E10"),sQuery(id+"F2.wireOp",EDGE,"E11"),sQuery(id+"F2.wireOp",EDGE,"E12")])],"isStart":true}),makeQuery(id+"F12.opExtrude","SWEPT_FACE",FACE,{"disambiguationData":[OSD([sQuery(id+"F11.wireOp",EDGE,"E19")])]})]});
            fillet(context, id + "F18", {"entities" : qUnion([Q0, Q1, Q2, Q3, Q4, Q5, Q6, Q7, Q8, Q9, Q10, Q11, Q12, Q13, Q14, Q15, Q16, Q17, Q18, Q19, Q20, Q21, Q22, Q23, Q24, Q25, Q26, Q27, Q28, Q29]), "radius" : 2.54 * mm, "tangentPropagation" : true, "allowEdgeOverflow" : false});
        }
        {
            var Q0;
            Q0=makeQuery(id+"F14.boolean.opBoolean","INTERSECT",EDGE,{"derivedFrom":[makeQuery(id+"F3.opExtrude","CAP_FACE",FACE,{"disambiguationData":[OSD([sQuery(id+"F2.wireOp",EDGE,"E8"),sQuery(id+"F2.wireOp",EDGE,"E9"),sQuery(id+"F2.wireOp",EDGE,"E10"),sQuery(id+"F2.wireOp",EDGE,"E11"),sQuery(id+"F2.wireOp",EDGE,"E12")])],"isStart":true}),makeQuery(id+"F14.opExtrude","SWEPT_FACE",FACE,{"disambiguationData":[OSD([sQuery(id+"F13.wireOp",EDGE,"E47")])]})]});
            var Q1;
            Q1=makeQuery(id+"F14.boolean.opBoolean","INTERSECT",EDGE,{"derivedFrom":[makeQuery(id+"F3.opExtrude","CAP_FACE",FACE,{"disambiguationData":[OSD([sQuery(id+"F2.wireOp",EDGE,"E8"),sQuery(id+"F2.wireOp",EDGE,"E9"),sQuery(id+"F2.wireOp",EDGE,"E10"),sQuery(id+"F2.wireOp",EDGE,"E11"),sQuery(id+"F2.wireOp",EDGE,"E12")])],"isStart":true}),makeQuery(id+"F14.opExtrude","SWEPT_FACE",FACE,{"disambiguationData":[OSD([sQuery(id+"F13.wireOp",EDGE,"E46")])]})]});
            var Q2;
            Q2=makeQuery(id+"F14.boolean.opBoolean","INTERSECT",EDGE,{"derivedFrom":[makeQuery(id+"F3.opExtrude","CAP_FACE",FACE,{"disambiguationData":[OSD([sQuery(id+"F2.wireOp",EDGE,"E8"),sQuery(id+"F2.wireOp",EDGE,"E9"),sQuery(id+"F2.wireOp",EDGE,"E10"),sQuery(id+"F2.wireOp",EDGE,"E11"),sQuery(id+"F2.wireOp",EDGE,"E12")])],"isStart":true}),makeQuery(id+"F14.opExtrude","SWEPT_FACE",FACE,{"disambiguationData":[OSD([sQuery(id+"F13.wireOp",EDGE,"E45")])]})]});
            var Q3;
            Q3=makeQuery(id+"F14.boolean.opBoolean","INTERSECT",EDGE,{"derivedFrom":[makeQuery(id+"F3.opExtrude","CAP_FACE",FACE,{"disambiguationData":[OSD([sQuery(id+"F2.wireOp",EDGE,"E8"),sQuery(id+"F2.wireOp",EDGE,"E9"),sQuery(id+"F2.wireOp",EDGE,"E10"),sQuery(id+"F2.wireOp",EDGE,"E11"),sQuery(id+"F2.wireOp",EDGE,"E12")])],"isStart":true}),makeQuery(id+"F14.opExtrude","SWEPT_FACE",FACE,{"disambiguationData":[OSD([sQuery(id+"F13.wireOp",EDGE,"E44")])]})]});
            var Q4;
            Q4=makeQuery(id+"F14.boolean.opBoolean","INTERSECT",EDGE,{"derivedFrom":[makeQuery(id+"F3.opExtrude","CAP_FACE",FACE,{"disambiguationData":[OSD([sQuery(id+"F2.wireOp",EDGE,"E8"),sQuery(id+"F2.wireOp",EDGE,"E9"),sQuery(id+"F2.wireOp",EDGE,"E10"),sQuery(id+"F2.wireOp",EDGE,"E11"),sQuery(id+"F2.wireOp",EDGE,"E12")])],"isStart":true}),makeQuery(id+"F14.opExtrude","SWEPT_FACE",FACE,{"disambiguationData":[OSD([sQuery(id+"F13.wireOp",EDGE,"E43")])]})]});
            var Q5;
            Q5=makeQuery(id+"F14.boolean.opBoolean","INTERSECT",EDGE,{"derivedFrom":[makeQuery(id+"F3.opExtrude","CAP_FACE",FACE,{"disambiguationData":[OSD([sQuery(id+"F2.wireOp",EDGE,"E8"),sQuery(id+"F2.wireOp",EDGE,"E9"),sQuery(id+"F2.wireOp",EDGE,"E10"),sQuery(id+"F2.wireOp",EDGE,"E11"),sQuery(id+"F2.wireOp",EDGE,"E12")])],"isStart":false}),makeQuery(id+"F14.opExtrude","SWEPT_FACE",FACE,{"disambiguationData":[OSD([sQuery(id+"F13.wireOp",EDGE,"E48")])]})]});
            var Q6;
            Q6=makeQuery(id+"F14.boolean.opBoolean","INTERSECT",EDGE,{"derivedFrom":[makeQuery(id+"F3.opExtrude","CAP_FACE",FACE,{"disambiguationData":[OSD([sQuery(id+"F2.wireOp",EDGE,"E8"),sQuery(id+"F2.wireOp",EDGE,"E9"),sQuery(id+"F2.wireOp",EDGE,"E10"),sQuery(id+"F2.wireOp",EDGE,"E11"),sQuery(id+"F2.wireOp",EDGE,"E12")])],"isStart":true}),makeQuery(id+"F14.opExtrude","SWEPT_FACE",FACE,{"disambiguationData":[OSD([sQuery(id+"F13.wireOp",EDGE,"E48")])]})]});
            var Q7;
            Q7=makeQuery(id+"F14.boolean.opBoolean","INTERSECT",EDGE,{"derivedFrom":[makeQuery(id+"F3.opExtrude","CAP_FACE",FACE,{"disambiguationData":[OSD([sQuery(id+"F2.wireOp",EDGE,"E8"),sQuery(id+"F2.wireOp",EDGE,"E9"),sQuery(id+"F2.wireOp",EDGE,"E10"),sQuery(id+"F2.wireOp",EDGE,"E11"),sQuery(id+"F2.wireOp",EDGE,"E12")])],"isStart":true}),makeQuery(id+"F14.opExtrude","SWEPT_FACE",FACE,{"disambiguationData":[OSD([sQuery(id+"F13.wireOp",EDGE,"E41")])]})]});
            var Q8;
            Q8=makeQuery(id+"F14.boolean.opBoolean","INTERSECT",EDGE,{"derivedFrom":[makeQuery(id+"F3.opExtrude","CAP_FACE",FACE,{"disambiguationData":[OSD([sQuery(id+"F2.wireOp",EDGE,"E8"),sQuery(id+"F2.wireOp",EDGE,"E9"),sQuery(id+"F2.wireOp",EDGE,"E10"),sQuery(id+"F2.wireOp",EDGE,"E11"),sQuery(id+"F2.wireOp",EDGE,"E12")])],"isStart":true}),makeQuery(id+"F14.opExtrude","SWEPT_FACE",FACE,{"disambiguationData":[OSD([sQuery(id+"F13.wireOp",EDGE,"E40")])]})]});
            var Q9;
            Q9=makeQuery(id+"F14.boolean.opBoolean","INTERSECT",EDGE,{"derivedFrom":[makeQuery(id+"F3.opExtrude","CAP_FACE",FACE,{"disambiguationData":[OSD([sQuery(id+"F2.wireOp",EDGE,"E8"),sQuery(id+"F2.wireOp",EDGE,"E9"),sQuery(id+"F2.wireOp",EDGE,"E10"),sQuery(id+"F2.wireOp",EDGE,"E11"),sQuery(id+"F2.wireOp",EDGE,"E12")])],"isStart":true}),makeQuery(id+"F14.opExtrude","SWEPT_FACE",FACE,{"disambiguationData":[OSD([sQuery(id+"F13.wireOp",EDGE,"E39")])]})]});
            var Q10;
            Q10=makeQuery(id+"F14.boolean.opBoolean","INTERSECT",EDGE,{"derivedFrom":[makeQuery(id+"F3.opExtrude","CAP_FACE",FACE,{"disambiguationData":[OSD([sQuery(id+"F2.wireOp",EDGE,"E8"),sQuery(id+"F2.wireOp",EDGE,"E9"),sQuery(id+"F2.wireOp",EDGE,"E10"),sQuery(id+"F2.wireOp",EDGE,"E11"),sQuery(id+"F2.wireOp",EDGE,"E12")])],"isStart":true}),makeQuery(id+"F14.opExtrude","SWEPT_FACE",FACE,{"disambiguationData":[OSD([sQuery(id+"F13.wireOp",EDGE,"E42")])]})]});
            var Q11;
            Q11=makeQuery(id+"F14.boolean.opBoolean","INTERSECT",EDGE,{"derivedFrom":[makeQuery(id+"F3.opExtrude","CAP_FACE",FACE,{"disambiguationData":[OSD([sQuery(id+"F2.wireOp",EDGE,"E8"),sQuery(id+"F2.wireOp",EDGE,"E9"),sQuery(id+"F2.wireOp",EDGE,"E10"),sQuery(id+"F2.wireOp",EDGE,"E11"),sQuery(id+"F2.wireOp",EDGE,"E12")])],"isStart":false}),makeQuery(id+"F14.opExtrude","SWEPT_FACE",FACE,{"disambiguationData":[OSD([sQuery(id+"F13.wireOp",EDGE,"E42")])]})]});
            var Q12;
            Q12=makeQuery(id+"F14.boolean.opBoolean","INTERSECT",EDGE,{"derivedFrom":[makeQuery(id+"F3.opExtrude","CAP_FACE",FACE,{"disambiguationData":[OSD([sQuery(id+"F2.wireOp",EDGE,"E8"),sQuery(id+"F2.wireOp",EDGE,"E9"),sQuery(id+"F2.wireOp",EDGE,"E10"),sQuery(id+"F2.wireOp",EDGE,"E11"),sQuery(id+"F2.wireOp",EDGE,"E12")])],"isStart":false}),makeQuery(id+"F14.opExtrude","SWEPT_FACE",FACE,{"disambiguationData":[OSD([sQuery(id+"F13.wireOp",EDGE,"E40")])]})]});
            var Q13;
            Q13=makeQuery(id+"F14.boolean.opBoolean","INTERSECT",EDGE,{"derivedFrom":[makeQuery(id+"F3.opExtrude","CAP_FACE",FACE,{"disambiguationData":[OSD([sQuery(id+"F2.wireOp",EDGE,"E8"),sQuery(id+"F2.wireOp",EDGE,"E9"),sQuery(id+"F2.wireOp",EDGE,"E10"),sQuery(id+"F2.wireOp",EDGE,"E11"),sQuery(id+"F2.wireOp",EDGE,"E12")])],"isStart":false}),makeQuery(id+"F14.opExtrude","SWEPT_FACE",FACE,{"disambiguationData":[OSD([sQuery(id+"F13.wireOp",EDGE,"E39")])]})]});
            var Q14;
            Q14=makeQuery(id+"F14.boolean.opBoolean","INTERSECT",EDGE,{"derivedFrom":[makeQuery(id+"F3.opExtrude","CAP_FACE",FACE,{"disambiguationData":[OSD([sQuery(id+"F2.wireOp",EDGE,"E8"),sQuery(id+"F2.wireOp",EDGE,"E9"),sQuery(id+"F2.wireOp",EDGE,"E10"),sQuery(id+"F2.wireOp",EDGE,"E11"),sQuery(id+"F2.wireOp",EDGE,"E12")])],"isStart":false}),makeQuery(id+"F14.opExtrude","SWEPT_FACE",FACE,{"disambiguationData":[OSD([sQuery(id+"F13.wireOp",EDGE,"E41")])]})]});
            var Q15;
            Q15=makeQuery(id+"F14.boolean.opBoolean","INTERSECT",EDGE,{"derivedFrom":[makeQuery(id+"F3.opExtrude","CAP_FACE",FACE,{"disambiguationData":[OSD([sQuery(id+"F2.wireOp",EDGE,"E8"),sQuery(id+"F2.wireOp",EDGE,"E9"),sQuery(id+"F2.wireOp",EDGE,"E10"),sQuery(id+"F2.wireOp",EDGE,"E11"),sQuery(id+"F2.wireOp",EDGE,"E12")])],"isStart":true}),makeQuery(id+"F14.opExtrude","SWEPT_FACE",FACE,{"disambiguationData":[OSD([sQuery(id+"F13.wireOp",EDGE,"E38")])]})]});
            var Q16;
            Q16=makeQuery(id+"F14.boolean.opBoolean","INTERSECT",EDGE,{"derivedFrom":[makeQuery(id+"F3.opExtrude","CAP_FACE",FACE,{"disambiguationData":[OSD([sQuery(id+"F2.wireOp",EDGE,"E8"),sQuery(id+"F2.wireOp",EDGE,"E9"),sQuery(id+"F2.wireOp",EDGE,"E10"),sQuery(id+"F2.wireOp",EDGE,"E11"),sQuery(id+"F2.wireOp",EDGE,"E12")])],"isStart":true}),makeQuery(id+"F14.opExtrude","SWEPT_FACE",FACE,{"disambiguationData":[OSD([sQuery(id+"F13.wireOp",EDGE,"E37")])]})]});
            var Q17;
            Q17=makeQuery(id+"F14.boolean.opBoolean","INTERSECT",EDGE,{"derivedFrom":[makeQuery(id+"F3.opExtrude","CAP_FACE",FACE,{"disambiguationData":[OSD([sQuery(id+"F2.wireOp",EDGE,"E8"),sQuery(id+"F2.wireOp",EDGE,"E9"),sQuery(id+"F2.wireOp",EDGE,"E10"),sQuery(id+"F2.wireOp",EDGE,"E11"),sQuery(id+"F2.wireOp",EDGE,"E12")])],"isStart":true}),makeQuery(id+"F14.opExtrude","SWEPT_FACE",FACE,{"disambiguationData":[OSD([sQuery(id+"F13.wireOp",EDGE,"E36")])]})]});
            var Q18;
            Q18=makeQuery(id+"F14.boolean.opBoolean","INTERSECT",EDGE,{"derivedFrom":[makeQuery(id+"F3.opExtrude","CAP_FACE",FACE,{"disambiguationData":[OSD([sQuery(id+"F2.wireOp",EDGE,"E8"),sQuery(id+"F2.wireOp",EDGE,"E9"),sQuery(id+"F2.wireOp",EDGE,"E10"),sQuery(id+"F2.wireOp",EDGE,"E11"),sQuery(id+"F2.wireOp",EDGE,"E12")])],"isStart":true}),makeQuery(id+"F14.opExtrude","SWEPT_FACE",FACE,{"disambiguationData":[OSD([sQuery(id+"F13.wireOp",EDGE,"E35")])]})]});
            var Q19;
            Q19=makeQuery(id+"F14.boolean.opBoolean","INTERSECT",EDGE,{"derivedFrom":[makeQuery(id+"F3.opExtrude","CAP_FACE",FACE,{"disambiguationData":[OSD([sQuery(id+"F2.wireOp",EDGE,"E8"),sQuery(id+"F2.wireOp",EDGE,"E9"),sQuery(id+"F2.wireOp",EDGE,"E10"),sQuery(id+"F2.wireOp",EDGE,"E11"),sQuery(id+"F2.wireOp",EDGE,"E12")])],"isStart":true}),makeQuery(id+"F14.opExtrude","SWEPT_FACE",FACE,{"disambiguationData":[OSD([sQuery(id+"F13.wireOp",EDGE,"E34")])]})]});
            var Q20;
            Q20=makeQuery(id+"F14.boolean.opBoolean","INTERSECT",EDGE,{"derivedFrom":[makeQuery(id+"F3.opExtrude","CAP_FACE",FACE,{"disambiguationData":[OSD([sQuery(id+"F2.wireOp",EDGE,"E8"),sQuery(id+"F2.wireOp",EDGE,"E9"),sQuery(id+"F2.wireOp",EDGE,"E10"),sQuery(id+"F2.wireOp",EDGE,"E11"),sQuery(id+"F2.wireOp",EDGE,"E12")])],"isStart":false}),makeQuery(id+"F14.opExtrude","SWEPT_FACE",FACE,{"disambiguationData":[OSD([sQuery(id+"F13.wireOp",EDGE,"E43")])]})]});
            var Q21;
            Q21=makeQuery(id+"F14.boolean.opBoolean","INTERSECT",EDGE,{"derivedFrom":[makeQuery(id+"F3.opExtrude","CAP_FACE",FACE,{"disambiguationData":[OSD([sQuery(id+"F2.wireOp",EDGE,"E8"),sQuery(id+"F2.wireOp",EDGE,"E9"),sQuery(id+"F2.wireOp",EDGE,"E10"),sQuery(id+"F2.wireOp",EDGE,"E11"),sQuery(id+"F2.wireOp",EDGE,"E12")])],"isStart":false}),makeQuery(id+"F14.opExtrude","SWEPT_FACE",FACE,{"disambiguationData":[OSD([sQuery(id+"F13.wireOp",EDGE,"E44")])]})]});
            var Q22;
            Q22=makeQuery(id+"F14.boolean.opBoolean","INTERSECT",EDGE,{"derivedFrom":[makeQuery(id+"F3.opExtrude","CAP_FACE",FACE,{"disambiguationData":[OSD([sQuery(id+"F2.wireOp",EDGE,"E8"),sQuery(id+"F2.wireOp",EDGE,"E9"),sQuery(id+"F2.wireOp",EDGE,"E10"),sQuery(id+"F2.wireOp",EDGE,"E11"),sQuery(id+"F2.wireOp",EDGE,"E12")])],"isStart":false}),makeQuery(id+"F14.opExtrude","SWEPT_FACE",FACE,{"disambiguationData":[OSD([sQuery(id+"F13.wireOp",EDGE,"E45")])]})]});
            var Q23;
            Q23=makeQuery(id+"F14.boolean.opBoolean","INTERSECT",EDGE,{"derivedFrom":[makeQuery(id+"F3.opExtrude","CAP_FACE",FACE,{"disambiguationData":[OSD([sQuery(id+"F2.wireOp",EDGE,"E8"),sQuery(id+"F2.wireOp",EDGE,"E9"),sQuery(id+"F2.wireOp",EDGE,"E10"),sQuery(id+"F2.wireOp",EDGE,"E11"),sQuery(id+"F2.wireOp",EDGE,"E12")])],"isStart":false}),makeQuery(id+"F14.opExtrude","SWEPT_FACE",FACE,{"disambiguationData":[OSD([sQuery(id+"F13.wireOp",EDGE,"E46")])]})]});
            var Q24;
            Q24=makeQuery(id+"F14.boolean.opBoolean","INTERSECT",EDGE,{"derivedFrom":[makeQuery(id+"F3.opExtrude","CAP_FACE",FACE,{"disambiguationData":[OSD([sQuery(id+"F2.wireOp",EDGE,"E8"),sQuery(id+"F2.wireOp",EDGE,"E9"),sQuery(id+"F2.wireOp",EDGE,"E10"),sQuery(id+"F2.wireOp",EDGE,"E11"),sQuery(id+"F2.wireOp",EDGE,"E12")])],"isStart":false}),makeQuery(id+"F14.opExtrude","SWEPT_FACE",FACE,{"disambiguationData":[OSD([sQuery(id+"F13.wireOp",EDGE,"E47")])]})]});
            var Q25;
            Q25=makeQuery(id+"F14.boolean.opBoolean","INTERSECT",EDGE,{"derivedFrom":[makeQuery(id+"F3.opExtrude","CAP_FACE",FACE,{"disambiguationData":[OSD([sQuery(id+"F2.wireOp",EDGE,"E8"),sQuery(id+"F2.wireOp",EDGE,"E9"),sQuery(id+"F2.wireOp",EDGE,"E10"),sQuery(id+"F2.wireOp",EDGE,"E11"),sQuery(id+"F2.wireOp",EDGE,"E12")])],"isStart":false}),makeQuery(id+"F14.opExtrude","SWEPT_FACE",FACE,{"disambiguationData":[OSD([sQuery(id+"F13.wireOp",EDGE,"E38")])]})]});
            var Q26;
            Q26=makeQuery(id+"F14.boolean.opBoolean","INTERSECT",EDGE,{"derivedFrom":[makeQuery(id+"F3.opExtrude","CAP_FACE",FACE,{"disambiguationData":[OSD([sQuery(id+"F2.wireOp",EDGE,"E8"),sQuery(id+"F2.wireOp",EDGE,"E9"),sQuery(id+"F2.wireOp",EDGE,"E10"),sQuery(id+"F2.wireOp",EDGE,"E11"),sQuery(id+"F2.wireOp",EDGE,"E12")])],"isStart":false}),makeQuery(id+"F14.opExtrude","SWEPT_FACE",FACE,{"disambiguationData":[OSD([sQuery(id+"F13.wireOp",EDGE,"E37")])]})]});
            var Q27;
            Q27=makeQuery(id+"F14.boolean.opBoolean","INTERSECT",EDGE,{"derivedFrom":[makeQuery(id+"F3.opExtrude","CAP_FACE",FACE,{"disambiguationData":[OSD([sQuery(id+"F2.wireOp",EDGE,"E8"),sQuery(id+"F2.wireOp",EDGE,"E9"),sQuery(id+"F2.wireOp",EDGE,"E10"),sQuery(id+"F2.wireOp",EDGE,"E11"),sQuery(id+"F2.wireOp",EDGE,"E12")])],"isStart":false}),makeQuery(id+"F14.opExtrude","SWEPT_FACE",FACE,{"disambiguationData":[OSD([sQuery(id+"F13.wireOp",EDGE,"E36")])]})]});
            var Q28;
            Q28=makeQuery(id+"F14.boolean.opBoolean","INTERSECT",EDGE,{"derivedFrom":[makeQuery(id+"F3.opExtrude","CAP_FACE",FACE,{"disambiguationData":[OSD([sQuery(id+"F2.wireOp",EDGE,"E8"),sQuery(id+"F2.wireOp",EDGE,"E9"),sQuery(id+"F2.wireOp",EDGE,"E10"),sQuery(id+"F2.wireOp",EDGE,"E11"),sQuery(id+"F2.wireOp",EDGE,"E12")])],"isStart":false}),makeQuery(id+"F14.opExtrude","SWEPT_FACE",FACE,{"disambiguationData":[OSD([sQuery(id+"F13.wireOp",EDGE,"E34")])]})]});
            var Q29;
            Q29=makeQuery(id+"F14.boolean.opBoolean","INTERSECT",EDGE,{"derivedFrom":[makeQuery(id+"F3.opExtrude","CAP_FACE",FACE,{"disambiguationData":[OSD([sQuery(id+"F2.wireOp",EDGE,"E8"),sQuery(id+"F2.wireOp",EDGE,"E9"),sQuery(id+"F2.wireOp",EDGE,"E10"),sQuery(id+"F2.wireOp",EDGE,"E11"),sQuery(id+"F2.wireOp",EDGE,"E12")])],"isStart":false}),makeQuery(id+"F14.opExtrude","SWEPT_FACE",FACE,{"disambiguationData":[OSD([sQuery(id+"F13.wireOp",EDGE,"E35")])]})]});
            fillet(context, id + "F19", {"entities" : qUnion([Q0, Q1, Q2, Q3, Q4, Q5, Q6, Q7, Q8, Q9, Q10, Q11, Q12, Q13, Q14, Q15, Q16, Q17, Q18, Q19, Q20, Q21, Q22, Q23, Q24, Q25, Q26, Q27, Q28, Q29]), "radius" : 2.54 * mm, "tangentPropagation" : true, "allowEdgeOverflow" : false});
        }
        {
            var Q0;
            Q0=qCreatedBy(makeId("Right.planeOp"),FACE);
            var sketch = newSketch(context, id + "F20", { "sketchPlane" : qUnion([Q0])});
            skCircle(sketch, "E79", {"center": v(-6.32, -48.15) * mm, "radius": 6.8 * mm});
            skSolve(sketch);
        }
        {
            var Q0;
            Q0=qSketchRegion(id+"F20",true);
            extrude(context, id + "F21", {"entities" : qUnion([Q0]), "operationType" : NewBodyOperationType.ADD, "depth" : 427.88 * mm, "hasSecondDirection" : true, "secondDirectionOppositeDirection" : false, "secondDirectionDepth" : 55.16 * mm});
        }
        {
            var Q0;
            Q0=makeQuery(id+"F21.opExtrude","CAP_FACE",FACE,{"disambiguationData":[OSD([sQuery(id+"F20.wireOp",EDGE,"E79")])],"isStart":false});
            var sketch = newSketch(context, id + "F22", { "sketchPlane" : qUnion([Q0])});
            skCircle(sketch, "E80", {"center": v(-6.32, -48.15) * mm, "radius": 22.23 * mm});
            skSolve(sketch);
        }
        {
            var Q0;
            Q0=qSketchRegion(id+"F22",true);
            extrude(context, id + "F23", {"entities" : qUnion([Q0]), "operationType" : NewBodyOperationType.ADD, "depth" : 25.4 * mm, "hasSecondDirection" : true, "secondDirectionOppositeDirection" : true, "secondDirectionDepth" : 138.2 * mm});
        }
        {
            var Q0;
            Q0=makeQuery(id+"F3.opExtrude","CAP_FACE",FACE,{"disambiguationData":[OSD([sQuery(id+"F2.wireOp",EDGE,"E8"),sQuery(id+"F2.wireOp",EDGE,"E9"),sQuery(id+"F2.wireOp",EDGE,"E10"),sQuery(id+"F2.wireOp",EDGE,"E11"),sQuery(id+"F2.wireOp",EDGE,"E12")])],"isStart":true});
            var sketch = newSketch(context, id + "F24", { "sketchPlane" : qUnion([Q0])});
            skLineSegment(sketch, "E81.bottom", {"start": v(-248.02, 86.34) * mm, "end": v(-338.98, 86.34) * mm});
            skLineSegment(sketch, "E81.top", {"start": v(-248.02, 52.26) * mm, "end": v(-338.98, 52.26) * mm});
            skLineSegment(sketch, "E81.left", {"start": v(-248.02, 86.34) * mm, "end": v(-248.02, 52.26) * mm});
            skLineSegment(sketch, "E81.right", {"start": v(-338.98, 86.34) * mm, "end": v(-338.98, 52.26) * mm});
            skSolve(sketch);
        }
        {
            var Q0;
            Q0=qSketchRegion(id+"F24",true);
            extrude(context, id + "F25", {"entities" : qUnion([Q0]), "operationType" : NewBodyOperationType.ADD, "depth" : 12.3 * mm});
        }
        {
            var Q0;
            Q0=makeQuery(id+"F25.opExtrude","SWEPT_EDGE",EDGE,{"disambiguationData":[OSD([sQuery(id+"F24.wireOp",EDGE,"E81.bottom"),sQuery(id+"F24.wireOp",EDGE,"E81.right")])]});
            var Q1;
            Q1=makeQuery(id+"F25.opExtrude","SWEPT_EDGE",EDGE,{"disambiguationData":[OSD([sQuery(id+"F24.wireOp",EDGE,"E81.top"),sQuery(id+"F24.wireOp",EDGE,"E81.right")])]});
            chamfer(context, id + "F26", {"entities" : qUnion([Q0, Q1]), "width" : 5.08 * mm, "tangentPropagation" : true});
        }
        {
            var Q0;
            Q0=qCreatedBy(makeId("Right.planeOp"),FACE);
            var sketch = newSketch(context, id + "F27", { "sketchPlane" : qUnion([Q0])});
            skCircle(sketch, "E82", {"center": v(54.58, 69.49) * mm, "radius": 18.96 * mm});
            skLineSegment(sketch, "E83", {"start": v(25.53, 81.36) * mm, "end": v(39.8, 81.36) * mm});
            skLineSegment(sketch, "E84", {"start": v(25.53, 57.22) * mm, "end": v(40.12, 57.22) * mm});
            skLineSegment(sketch, "E85", {"start": v(25.53, 81.36) * mm, "end": v(25.53, 57.22) * mm});
            skCircle(sketch, "E86", {"center": v(54.58, 69.49) * mm, "radius": 16.75 * mm});
            skSolve(sketch);
        }
        {
            var Q0;
            Q0=qSketchRegion(id+"F27",true);
            extrude(context, id + "F28", {"entities" : qUnion([Q0]), "operationType" : NewBodyOperationType.ADD, "depth" : 339.09 * mm, "hasSecondDirection" : true, "secondDirectionOppositeDirection" : false, "secondDirectionDepth" : 252.93 * mm});
        }
        {
            var Q0;
            Q0=makeQuery(id+"F25.opExtrude","SWEPT_EDGE",EDGE,{"disambiguationData":[OSD([sQuery(id+"F24.wireOp",EDGE,"E81.bottom"),sQuery(id+"F24.wireOp",EDGE,"E81.left")])]});
            var Q1;
            Q1=makeQuery(id+"F25.opExtrude","SWEPT_EDGE",EDGE,{"disambiguationData":[OSD([sQuery(id+"F24.wireOp",EDGE,"E81.top"),sQuery(id+"F24.wireOp",EDGE,"E81.left")])]});
            chamfer(context, id + "F29", {"entities" : qUnion([Q0, Q1]), "width" : 5.08 * mm, "tangentPropagation" : true});
        }
        {
            var Q0;
            Q0=qCreatedBy(makeId("Front.planeOp"),FACE);
            var sketch = newSketch(context, id + "F30", { "sketchPlane" : qUnion([Q0])});
            skLineSegment(sketch, "E87", {"start": v(-35.01, 618.44) * mm, "end": v(-35.01, -645.7) * mm});
            skLineSegment(sketch, "E88.0", {"start": v(-33.41, 618.44) * mm, "end": v(-33.41, -645.7) * mm});
            skSolve(sketch);
        }
        {
            var Q0;
            Q0=sQuery(id+"F30.wireOp",EDGE,"E88.0");
            var Q1;
            Q1=sQuery(id+"F30.wireOp",EDGE,"E87");
            revolve(context, id + "F31", {"bodyType" : ToolBodyType.SURFACE, "surfaceEntities" : qUnion([Q0]), "axis" : qUnion([Q1]), "revolveType" : RevolveType.FULL});
        }
        {
            var Q0;
            Q0=makeQuery(id+"F21.opExtrude","CAP_FACE",FACE,{"disambiguationData":[OSD([sQuery(id+"F20.wireOp",EDGE,"E79")])],"isStart":true});
            var sketch = newSketch(context, id + "F32", { "sketchPlane" : qUnion([Q0])});
            skCircle(sketch, "E89", {"center": v(6.32, -48.15) * mm, "radius": 7.8 * mm});
            skSolve(sketch);
        }
        {
            var Q0;
            Q0=makeQuery(id+"F32.imprint","IMPRINT",FACE,{"disambiguationData":[TD([[makeQuery(id+"F32.imprint","IMPRINT",EDGE,{"derivedFrom":sQuery(id+"F32.wireOp",EDGE,"E89")}),1.0]])]});
            extrude(context, id + "F33", {"entities" : qUnion([Q0]), "operationType" : NewBodyOperationType.ADD, "oppositeDirection" : true, "depth" : 44.82 * mm, "hasSecondDirection" : true, "secondDirectionOppositeDirection" : true, "secondDirectionDepth" : 25.57 * mm});
        }
        {
            var Q0;
            Q0=qCreatedBy(makeId("Front.planeOp"),FACE);
            var sketch = newSketch(context, id + "F34", { "sketchPlane" : qUnion([Q0])});
            skLineSegment(sketch, "E90.bottom", {"start": v(82.17, -43.31) * mm, "end": v(98.27, -43.31) * mm});
            skLineSegment(sketch, "E90.top", {"start": v(82.17, -52.61) * mm, "end": v(98.27, -52.61) * mm});
            skLineSegment(sketch, "E90.left", {"start": v(82.17, -43.31) * mm, "end": v(82.17, -52.61) * mm});
            skLineSegment(sketch, "E90.right", {"start": v(98.27, -43.31) * mm, "end": v(98.27, -52.61) * mm});
            skSolve(sketch);
        }
        {
            var Q0;
            Q0=qSketchRegion(id+"F34",true);
            extrude(context, id + "F35", {"entities" : qUnion([Q0]), "operationType" : NewBodyOperationType.ADD, "depth" : 25.4 * mm, "hasSecondDirection" : true, "secondDirectionOppositeDirection" : false, "secondDirectionDepth" : 9.5 * mm});
        }
        {
            var Q0;
            Q0=qCreatedBy(makeId("Top.planeOp"),FACE);
            var sketch = newSketch(context, id + "F36", { "sketchPlane" : qUnion([Q0])});
            skCircle(sketch, "E91", {"center": v(85.28, -21.16) * mm, "radius": 2.19 * mm});
            skCircle(sketch, "E92", {"center": v(93.2, -20.96) * mm, "radius": 2.28 * mm});
            skSolve(sketch);
        }
        {
            var Q0;
            Q0=qSketchRegion(id+"F36",true);
            extrude(context, id + "F37", {"entities" : qUnion([Q0]), "operationType" : NewBodyOperationType.REMOVE, "depth" : 25.4 * mm, "hasSecondDirection" : true, "secondDirectionOppositeDirection" : true, "secondDirectionDepth" : 80.47 * mm});
        }
        {
            var Q0;
            Q0=qCreatedBy(makeId("Right.planeOp"),FACE);
            var sketch = newSketch(context, id + "F38", { "sketchPlane" : qUnion([Q0])});
            skLineSegment(sketch, "E93.bottom", {"start": v(48.45, 45.7) * mm, "end": v(0, 45.7) * mm});
            skLineSegment(sketch, "E93.top", {"start": v(48.45, 6.44) * mm, "end": v(0, 6.44) * mm});
            skLineSegment(sketch, "E93.left", {"start": v(48.45, 45.7) * mm, "end": v(48.45, 6.44) * mm});
            skLineSegment(sketch, "E93.right", {"start": v(0, 45.7) * mm, "end": v(0, 6.44) * mm});
            skSolve(sketch);
        }
        {
            var Q0;
            Q0 = qSketchRegion(id + "F38", true);
            extrude(context, id + "F39", {"entities" : qUnion([Q0]), "operationType" : NewBodyOperationType.REMOVE, "oppositeDirection" : true, "depth" : 25.4 * mm, "hasSecondDirection" : true, "secondDirectionOppositeDirection" : false, "secondDirectionDepth" : 467.55 * mm});
        }
        {
            var Q0;
            Q0=qCreatedBy(makeId("Right.planeOp"),FACE);
            var sketch = newSketch(context, id + "F40", { "sketchPlane" : qUnion([Q0])});
            skLineSegment(sketch, "E94.bottom", {"start": v(0, 45.7) * mm, "end": v(39.96, 45.7) * mm});
            skLineSegment(sketch, "E94.top", {"start": v(0, 6.43) * mm, "end": v(39.96, 6.43) * mm});
            skLineSegment(sketch, "E94.left", {"start": v(0, 45.7) * mm, "end": v(0, 6.43) * mm});
            skLineSegment(sketch, "E94.right", {"start": v(39.96, 45.7) * mm, "end": v(39.96, 6.43) * mm});
            skLineSegment(sketch, "E95.bottom", {"start": v(38.21, 43.95) * mm, "end": v(1.74, 43.95) * mm});
            skLineSegment(sketch, "E95.top", {"start": v(38.21, 7.95) * mm, "end": v(1.74, 7.95) * mm});
            skLineSegment(sketch, "E95.left", {"start": v(38.21, 43.95) * mm, "end": v(38.21, 7.95) * mm});
            skLineSegment(sketch, "E95.right", {"start": v(1.74, 43.95) * mm, "end": v(1.74, 7.95) * mm});
            skSolve(sketch);
        }
        {
            var Q0;
            Q0 = qSketchRegion(id + "F40", true);
            extrude(context, id + "F41", {"entities" : qUnion([Q0]), "operationType" : NewBodyOperationType.ADD, "depth" : 364.2 * mm, "hasSecondDirection" : true, "secondDirectionOppositeDirection" : false, "secondDirectionDepth" : 142.02 * mm});
        }
        {
            var Q0;
            Q0=qCreatedBy(makeId("Right.planeOp"),FACE);
            var sketch = newSketch(context, id + "F42", { "sketchPlane" : qUnion([Q0])});
            skLineSegment(sketch, "E96.bottom", {"start": v(48.03, 34.83) * mm, "end": v(31.03, 34.83) * mm});
            skLineSegment(sketch, "E96.top", {"start": v(48.03, 16) * mm, "end": v(31.03, 16) * mm});
            skLineSegment(sketch, "E96.left", {"start": v(48.03, 34.83) * mm, "end": v(48.03, 16) * mm});
            skLineSegment(sketch, "E96.right", {"start": v(31.03, 34.83) * mm, "end": v(31.03, 16) * mm});
            skSolve(sketch);
        }
        {
            var Q0;
            Q0 = qSketchRegion(id + "F42", true);
            extrude(context, id + "F43", {"entities" : qUnion([Q0]), "operationType" : NewBodyOperationType.REMOVE, "oppositeDirection" : true, "depth" : 25.4 * mm, "hasSecondDirection" : true, "secondDirectionOppositeDirection" : false, "secondDirectionDepth" : 376.23 * mm});
        }
        {
            var Q0;
            Q0=qCreatedBy(makeId("Front.planeOp"),FACE);
            var sketch = newSketch(context, id + "F44", { "sketchPlane" : qUnion([Q0])});
            skLineSegment(sketch, "E97.bottom", {"start": v(364.1, 15.69) * mm, "end": v(142.13, 15.69) * mm});
            skLineSegment(sketch, "E97.top", {"start": v(364.1, -91.71) * mm, "end": v(142.13, -91.71) * mm});
            skLineSegment(sketch, "E97.left", {"start": v(364.1, 15.69) * mm, "end": v(364.1, -91.71) * mm});
            skLineSegment(sketch, "E97.right", {"start": v(142.13, 15.69) * mm, "end": v(142.13, -91.71) * mm});
            skSolve(sketch);
        }
        {
            var Q0;
            Q0 = qSketchRegion(id + "F44", true);
            extrude(context, id + "F45", {"entities" : qUnion([Q0]), "operationType" : NewBodyOperationType.ADD, "oppositeDirection" : true, "depth" : 48.42 * mm, "hasSecondDirection" : true, "secondDirectionOppositeDirection" : true, "secondDirectionDepth" : 38.6 * mm});
        }
        {
            var Q0;
            Q0=qCreatedBy(makeId("Right.planeOp"),FACE);
            var sketch = newSketch(context, id + "F46", { "sketchPlane" : qUnion([Q0])});
            skCircle(sketch, "E98", {"center": v(45.15, 8.8) * mm, "radius": 4.2 * mm});
            skCircle(sketch, "E99", {"center": v(45.15, -5.11) * mm, "radius": 4.57 * mm});
            skCircle(sketch, "E100", {"center": v(45.15, -19.42) * mm, "radius": 4.34 * mm});
            skCircle(sketch, "E101", {"center": v(45.15, -31.96) * mm, "radius": 4.32 * mm});
            skCircle(sketch, "E102", {"center": v(45.15, -46.46) * mm, "radius": 4.35 * mm});
            skCircle(sketch, "E103", {"center": v(45.15, -60.37) * mm, "radius": 4.71 * mm});
            skCircle(sketch, "E104", {"center": v(45.15, -74.48) * mm, "radius": 4.4 * mm});
            skCircle(sketch, "E105", {"center": v(45.15, -86.83) * mm, "radius": 3.94 * mm});
            skSolve(sketch);
        }
        {
            var Q0;
            Q0 = qSketchRegion(id + "F46", true);
            extrude(context, id + "F47", {"entities" : qUnion([Q0]), "operationType" : NewBodyOperationType.REMOVE, "oppositeDirection" : true, "depth" : 25.4 * mm, "hasSecondDirection" : true, "secondDirectionOppositeDirection" : false, "secondDirectionDepth" : 642.35 * mm});
        }
        {
            var Q0;
            Q0=qCreatedBy(makeId("Right.planeOp"),FACE);
            var sketch = newSketch(context, id + "F48", { "sketchPlane" : qUnion([Q0])});
            skLineSegment(sketch, "E106", {"start": v(24.17, 7.68) * mm, "end": v(24.17, 12.91) * mm});
            skLineSegment(sketch, "E107.0", {"start": v(17.82, 7.6) * mm, "end": v(17.82, 12.7) * mm});
            skLineSegment(sketch, "E108", {"start": v(17.82, 12.7) * mm, "end": v(16.33, 16.65) * mm});
            skLineSegment(sketch, "E109", {"start": v(24.17, 12.91) * mm, "end": v(25.97, 16.3) * mm});
            skLineSegment(sketch, "E110", {"start": v(25.97, 16.3) * mm, "end": v(20.85, 12.91) * mm});
            skLineSegment(sketch, "E111", {"start": v(20.85, 12.91) * mm, "end": v(16.33, 16.65) * mm});
            skLineSegment(sketch, "E112", {"start": v(24.17, 7.68) * mm, "end": v(17.82, 7.6) * mm});
            skSolve(sketch);
        }
        {
            var Q0;
            Q0 = qSketchRegion(id + "F48", true);
            extrude(context, id + "F49", {"entities" : qUnion([Q0]), "operationType" : NewBodyOperationType.ADD, "depth" : 363.34 * mm, "hasSecondDirection" : true, "secondDirectionOppositeDirection" : false, "secondDirectionDepth" : 142.07 * mm});
        }
        {
            var Q0;
            Q0 = qSketchRegion(id + "F15", true);
            extrude(context, id + "F50", {"entities" : qUnion([Q0]), "operationType" : NewBodyOperationType.ADD, "depth" : 13.02 * mm});
        }
        {
            var Q0;
            Q0=qCreatedBy(makeId("Top.planeOp"),FACE);
            var sketch = newSketch(context, id + "F51", { "sketchPlane" : qUnion([Q0])});
            skCircle(sketch, "E113", {"center": v(-27.12, -6.5) * mm, "radius": 4.63 * mm});
            skSolve(sketch);
        }
        {
            var Q0;
            Q0 = qSketchRegion(id + "F51", true);
            extrude(context, id + "F52", {"entities" : qUnion([Q0]), "operationType" : NewBodyOperationType.ADD, "depth" : 601.46 * mm, "hasSecondDirection" : true, "secondDirectionOppositeDirection" : true, "secondDirectionDepth" : 631.8 * mm});
        }
    });
